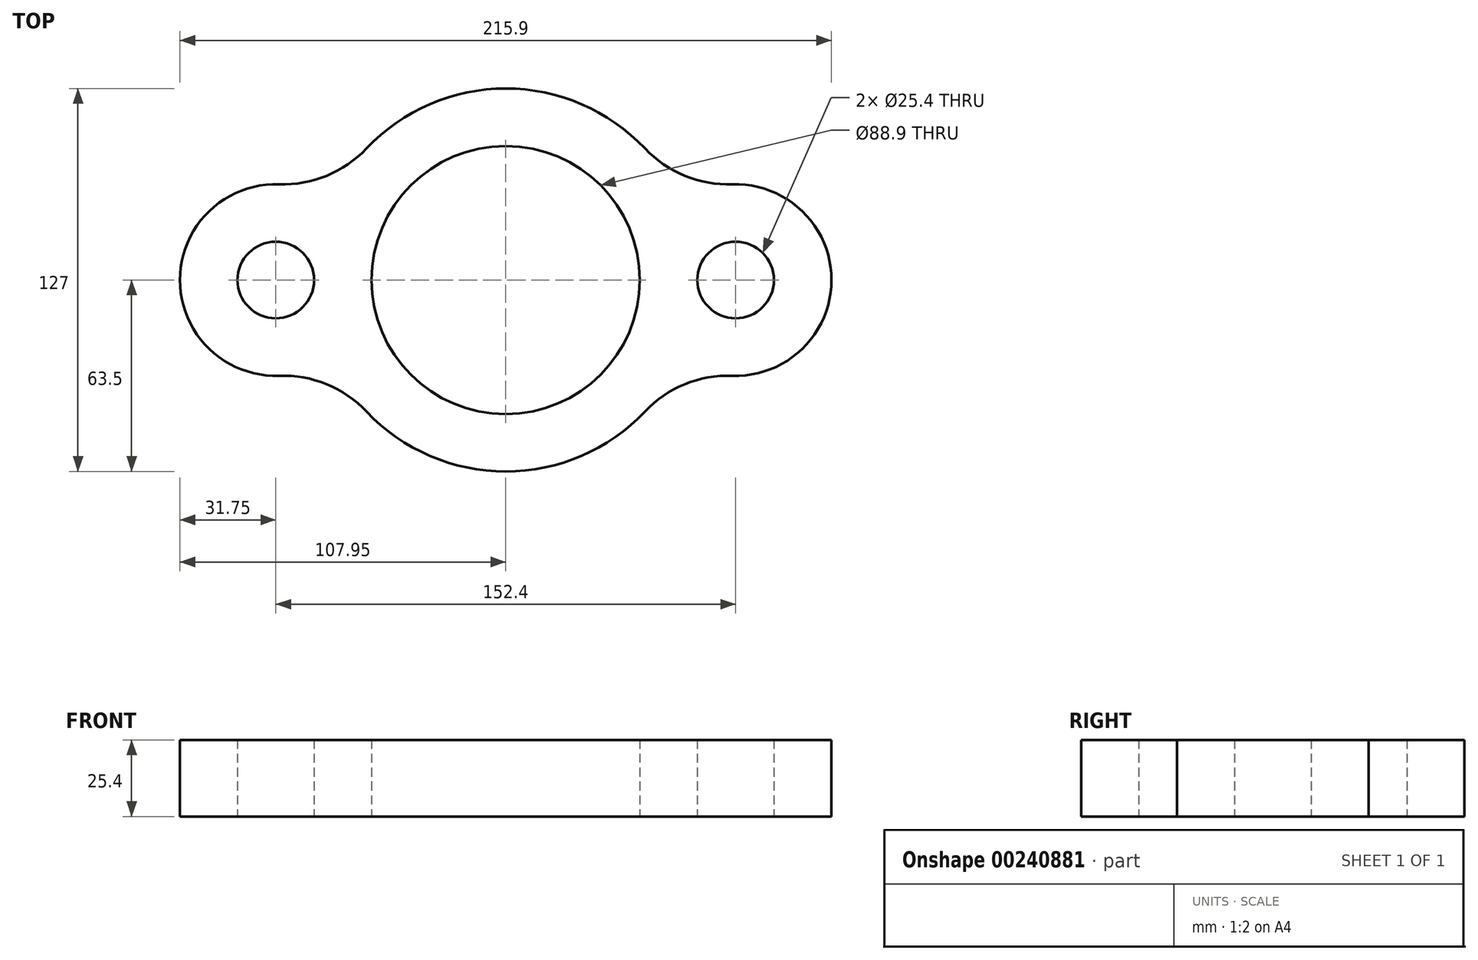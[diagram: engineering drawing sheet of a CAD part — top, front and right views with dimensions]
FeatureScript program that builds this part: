
annotation { "Feature Type Name" : "Feature", "Feature Type Description" : "" }
export const myFeature = defineFeature(function(context is Context, id is Id, definition is map)
    precondition{}
    {
        {
            var Q0;
            Q0=qCreatedBy(makeId("Top.planeOp"),FACE);
            var sketch = newSketch(context, id + "F0", { "sketchPlane" : qUnion([Q0])});
            skCircle(sketch, "E0", {"center": v(0, 0) * mm, "radius": 44.45 * mm});
            skArc(sketch, "E1", {"start": v(46.14, 43.63) * mm, "mid": v(0, 63.5) * mm, "end": v(-46.14, 43.63) * mm});
            skCircle(sketch, "E2", {"center": v(76.2, 0) * mm, "radius": 12.7 * mm});
            skArc(sketch, "E3", {"start": v(75.12, -31.73) * mm, "mid": v(107.95, 0) * mm, "end": v(75.12, 31.73) * mm});
            skArc(sketch, "E4", {"start": v(46.14, 43.63) * mm, "mid": v(59.35, 34.56) * mm, "end": v(75.12, 31.73) * mm});
            skArc(sketch, "E5", {"start": v(75.12, -31.73) * mm, "mid": v(59.35, -34.56) * mm, "end": v(46.14, -43.63) * mm});
            skCircle(sketch, "E6", {"center": v(-76.2, 0) * mm, "radius": 12.7 * mm});
            skArc(sketch, "E7", {"start": v(-75.12, 31.73) * mm, "mid": v(-107.95, 0) * mm, "end": v(-75.12, -31.73) * mm});
            skArc(sketch, "E8", {"start": v(-75.12, 31.73) * mm, "mid": v(-59.35, 34.56) * mm, "end": v(-46.14, 43.63) * mm});
            skArc(sketch, "E9.trimOffspring", {"start": v(-46.14, -43.63) * mm, "mid": v(0, -63.5) * mm, "end": v(46.14, -43.63) * mm});
            skArc(sketch, "E10", {"start": v(-46.14, -43.63) * mm, "mid": v(-59.35, -34.56) * mm, "end": v(-75.12, -31.73) * mm});
            skSolve(sketch);
        }
        {
            var Q0;
            Q0=makeQuery(id+"F0.imprint","IMPRINT",FACE,{"disambiguationData":[TD([[makeQuery(id+"F0.imprint","IMPRINT",EDGE,{"derivedFrom":sQuery(id+"F0.wireOp",EDGE,"E0")}),-1.0]])]});
            extrude(context, id + "F1", {"entities" : qUnion([Q0]), "depth" : 25.4 * mm});
        }
    });
